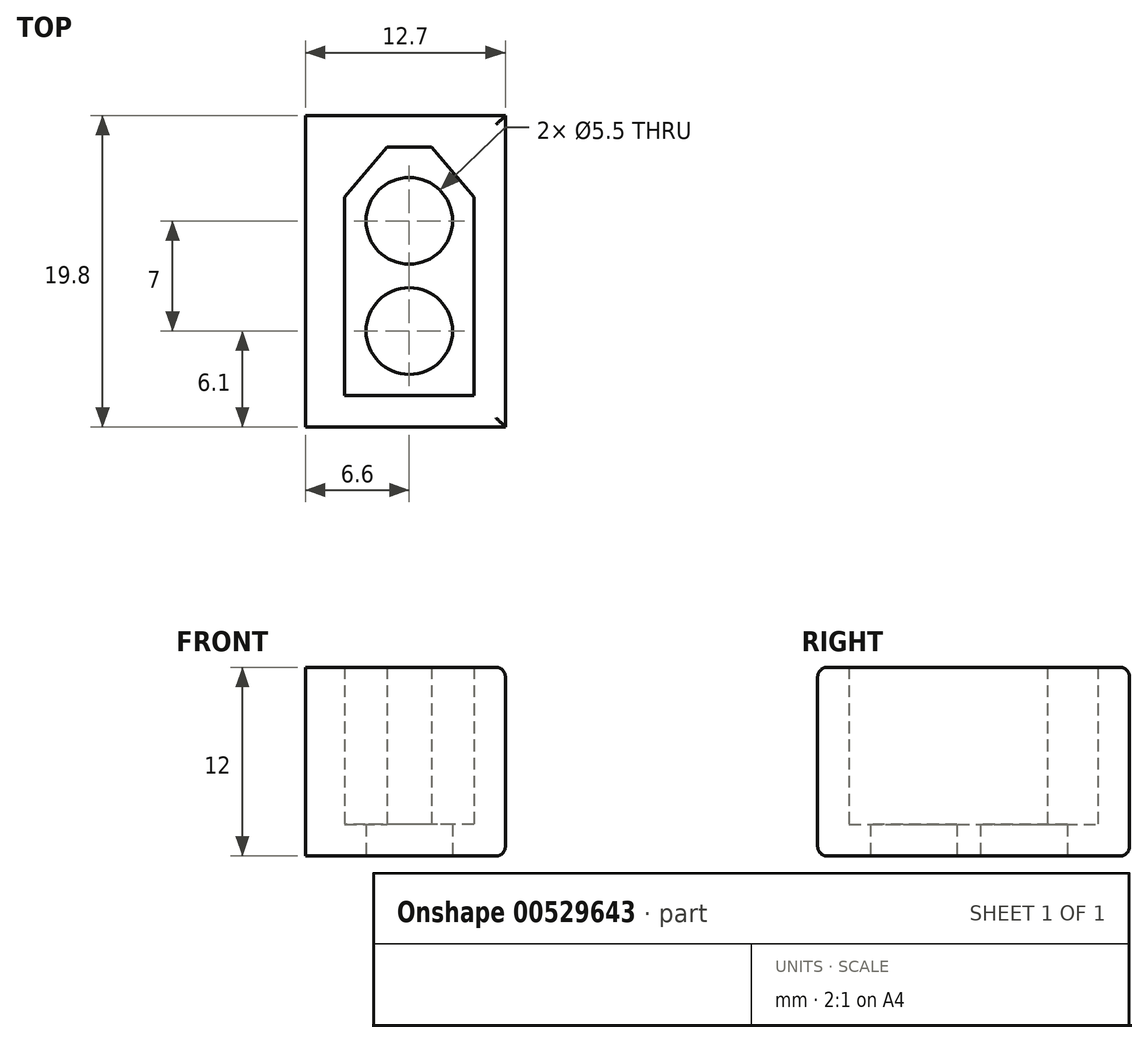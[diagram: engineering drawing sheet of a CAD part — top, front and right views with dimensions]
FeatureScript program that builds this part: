
annotation { "Feature Type Name" : "Feature", "Feature Type Description" : "" }
export const myFeature = defineFeature(function(context is Context, id is Id, definition is map)
    precondition{}
    {
        {
            var Q0;
            Q0=qCreatedBy(makeId("Top.planeOp"),FACE);
            var sketch = newSketch(context, id + "F0", { "sketchPlane" : qUnion([Q0])});
            skLineSegment(sketch, "E0.bottom", {"start": v(7.1, 0) * mm, "end": v(19.8, 0) * mm});
            skLineSegment(sketch, "E0.top", {"start": v(4.55, 19.8) * mm, "end": v(19.8, 19.8) * mm});
            skLineSegment(sketch, "E0.right", {"start": v(19.8, 0) * mm, "end": v(19.8, 19.8) * mm});
            skLineSegment(sketch, "E1.bottom", {"start": v(17.8, 2) * mm, "end": v(9.6, 2) * mm});
            skLineSegment(sketch, "E1.top", {"start": v(15.1, 17.8) * mm, "end": v(12.3, 17.8) * mm});
            skLineSegment(sketch, "E1.left", {"start": v(17.8, 2) * mm, "end": v(17.8, 14.6) * mm});
            skLineSegment(sketch, "E1.right", {"start": v(9.6, 2) * mm, "end": v(9.6, 14.6) * mm});
            skLineSegment(sketch, "E2", {"start": v(17.8, 14.6) * mm, "end": v(15.1, 17.8) * mm});
            skLineSegment(sketch, "E3", {"start": v(9.6, 14.6) * mm, "end": v(12.3, 17.8) * mm});
            skPoint(sketch, "E4.orphan", {"position": v(17.8, 17.8) * mm});
            skLineSegment(sketch, "E5", {"start": v(13.7, 2) * mm, "end": v(13.7, 24.2) * mm, "construction": true});
            skCircle(sketch, "E6", {"center": v(13.7, 6.1) * mm, "radius": 2.75 * mm});
            skCircle(sketch, "E7", {"center": v(13.7, 13.1) * mm, "radius": 2.75 * mm});
            skLineSegment(sketch, "E8", {"start": v(7.1, 0) * mm, "end": v(7.1, 25.9) * mm, "construction": true});
            skLineSegment(sketch, "E9", {"start": v(4.55, 5.61) * mm, "end": v(4.55, 23.27) * mm, "construction": true});
            skLineSegment(sketch, "E10", {"start": v(7.1, 19.8) * mm, "end": v(7.1, 0) * mm});
            skSolve(sketch);
        }
        {
            var Q0;
            Q0=makeQuery(id+"F0.imprint","IMPRINT",FACE,{"disambiguationData":[TD([[makeQuery(id+"F0.imprint","IMPRINT",EDGE,{"derivedFrom":sQuery(id+"F0.wireOp",EDGE,"E0.bottom")}),1.0]])]});
            extrude(context, id + "F1", {"entities" : qUnion([Q0]), "depth" : 12 * mm});
        }
        {
            var Q0;
            Q0=makeQuery(id+"F0.imprint","IMPRINT",FACE,{"disambiguationData":[TD([[makeQuery(id+"F0.imprint","IMPRINT",EDGE,{"derivedFrom":sQuery(id+"F0.wireOp",EDGE,"E1.bottom")}),-1.0]])]});
            extrude(context, id + "F2", {"entities" : qUnion([Q0]), "operationType" : NewBodyOperationType.ADD, "depth" : 2 * mm});
        }
        {
            var Q0;
            Q0=makeQuery(id+"F1.opExtrude","CAP_EDGE",EDGE,{"disambiguationData":[OSD([sQuery(id+"F0.wireOp",EDGE,"E0.bottom")])],"isStart":false});
            var Q1;
            Q1=makeQuery(id+"F1.opExtrude","CAP_EDGE",EDGE,{"disambiguationData":[OSD([sQuery(id+"F0.wireOp",EDGE,"E0.right")])],"isStart":false});
            var Q2;
            Q2=makeQuery(id+"F1.opExtrude","CAP_EDGE",EDGE,{"disambiguationData":[OSD([sQuery(id+"F0.wireOp",EDGE,"E0.top")])],"isStart":false});
            var Q3;
            Q3=makeQuery(id+"F1.opExtrude","CAP_EDGE",EDGE,{"disambiguationData":[OSD([sQuery(id+"F0.wireOp",EDGE,"E0.left")])],"isStart":false});
            fillet(context, id + "F3", {"entities" : qUnion([Q0, Q1, Q2, Q3]), "radius" : .6 * mm, "tangentPropagation" : true, "allowEdgeOverflow" : false});
        }
        {
            var Q0;
            Q0=makeQuery(id+"F1.opExtrude","CAP_EDGE",EDGE,{"disambiguationData":[OSD([sQuery(id+"F0.wireOp",EDGE,"E0.bottom")])],"isStart":true});
            var Q1;
            Q1=makeQuery(id+"F1.opExtrude","CAP_EDGE",EDGE,{"disambiguationData":[OSD([sQuery(id+"F0.wireOp",EDGE,"E0.right")])],"isStart":true});
            var Q2;
            Q2=makeQuery(id+"F1.opExtrude","CAP_EDGE",EDGE,{"disambiguationData":[OSD([sQuery(id+"F0.wireOp",EDGE,"E0.top")])],"isStart":true});
            var Q3;
            Q3=makeQuery(id+"F1.opExtrude","CAP_EDGE",EDGE,{"disambiguationData":[OSD([sQuery(id+"F0.wireOp",EDGE,"E0.left")])],"isStart":true});
            fillet(context, id + "F4", {"entities" : qUnion([Q0, Q1, Q2, Q3]), "radius" : .6 * mm, "tangentPropagation" : true, "allowEdgeOverflow" : false});
        }
    });
